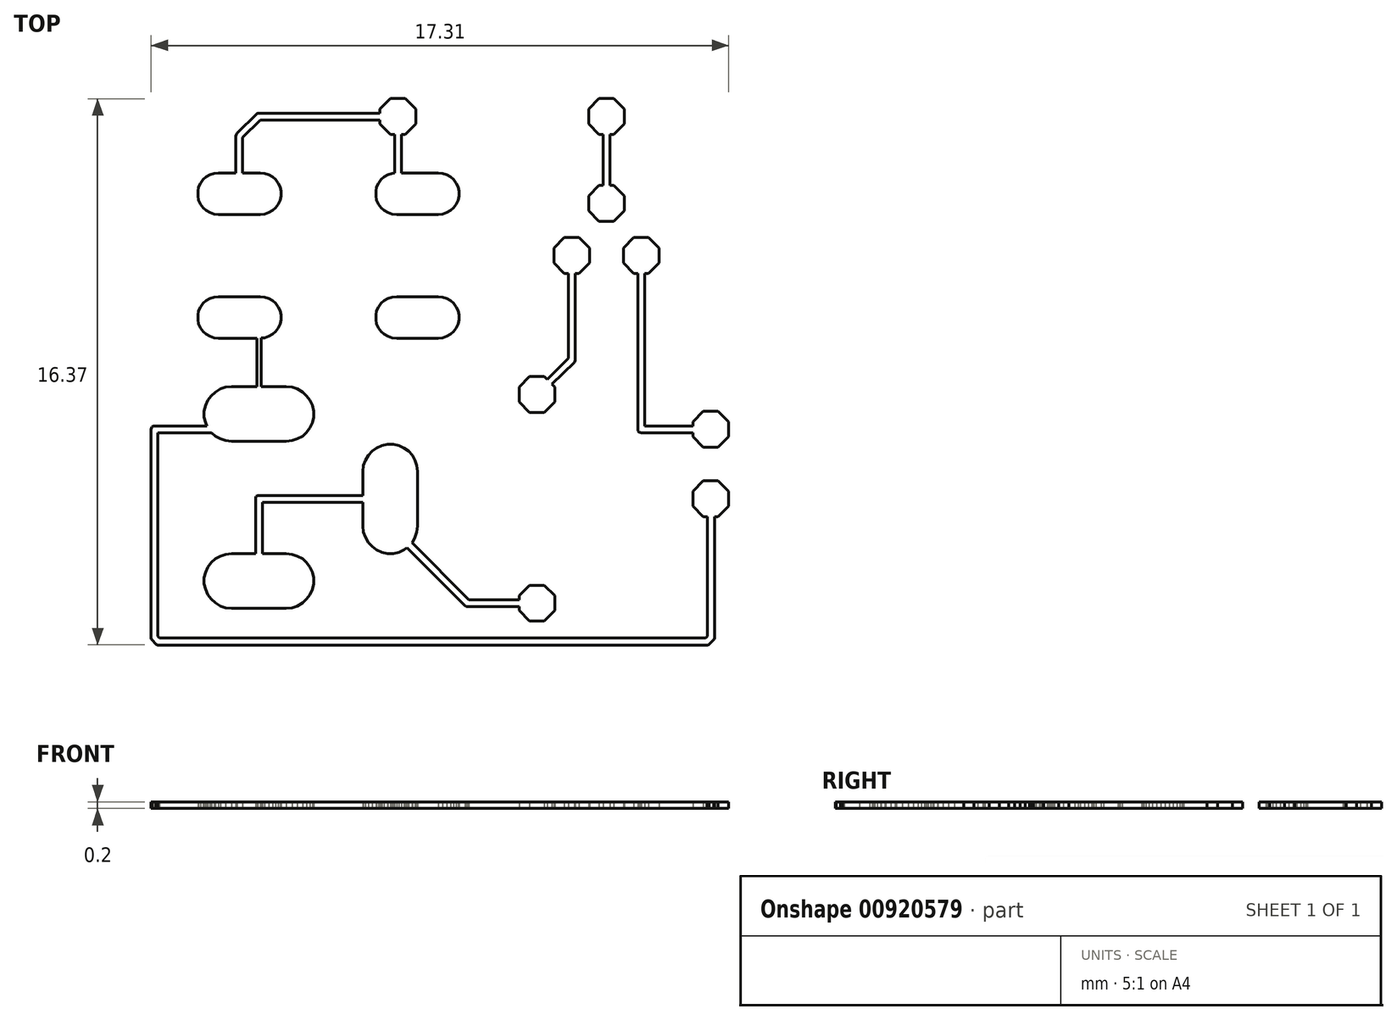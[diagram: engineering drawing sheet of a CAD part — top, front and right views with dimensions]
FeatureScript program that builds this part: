
annotation { "Feature Type Name" : "Feature", "Feature Type Description" : "" }
export const myFeature = defineFeature(function(context is Context, id is Id, definition is map)
    precondition{}
    {
        {
            var Q0;
            Q0=qCreatedBy(makeId("Top.planeOp"),FACE);
            var sketch = newSketch(context, id + "F0", { "sketchPlane" : qUnion([Q0])});
            skLineSegment(sketch, "E0", {"start": v(-0.87, 0.65) * mm, "end": v(-2.12, 0.65) * mm});
            skLineSegment(sketch, "E1", {"start": v(-2.12, 0.65) * mm, "end": v(-2.26, 0.67) * mm});
            skLineSegment(sketch, "E2", {"start": v(-2.26, 0.67) * mm, "end": v(-2.38, 0.7) * mm});
            skLineSegment(sketch, "E3", {"start": v(-2.38, 0.7) * mm, "end": v(-2.5, 0.77) * mm});
            skLineSegment(sketch, "E4", {"start": v(-2.5, 0.77) * mm, "end": v(-2.59, 0.85) * mm});
            skLineSegment(sketch, "E5", {"start": v(-2.59, 0.85) * mm, "end": v(-2.66, 0.96) * mm});
            skLineSegment(sketch, "E6", {"start": v(-2.66, 0.96) * mm, "end": v(-2.72, 1.08) * mm});
            skLineSegment(sketch, "E7", {"start": v(-2.72, 1.08) * mm, "end": v(-2.74, 1.2) * mm});
            skLineSegment(sketch, "E8", {"start": v(-2.74, 1.2) * mm, "end": v(-2.74, 1.34) * mm});
            skLineSegment(sketch, "E9", {"start": v(-2.74, 1.34) * mm, "end": v(-2.72, 1.47) * mm});
            skLineSegment(sketch, "E10", {"start": v(-2.72, 1.47) * mm, "end": v(-2.66, 1.58) * mm});
            skLineSegment(sketch, "E11", {"start": v(-2.66, 1.58) * mm, "end": v(-2.59, 1.7) * mm});
            skLineSegment(sketch, "E12", {"start": v(-2.59, 1.7) * mm, "end": v(-2.5, 1.78) * mm});
            skLineSegment(sketch, "E13", {"start": v(-2.5, 1.78) * mm, "end": v(-2.38, 1.84) * mm});
            skLineSegment(sketch, "E14", {"start": v(-2.38, 1.84) * mm, "end": v(-2.26, 1.89) * mm});
            skLineSegment(sketch, "E15", {"start": v(-2.26, 1.89) * mm, "end": v(-2.12, 1.9) * mm});
            skLineSegment(sketch, "E16", {"start": v(-2.12, 1.9) * mm, "end": v(-0.87, 1.9) * mm});
            skLineSegment(sketch, "E17", {"start": v(-0.87, 1.9) * mm, "end": v(-0.74, 1.89) * mm});
            skLineSegment(sketch, "E18", {"start": v(-0.74, 1.89) * mm, "end": v(-0.62, 1.84) * mm});
            skLineSegment(sketch, "E19", {"start": v(-0.62, 1.84) * mm, "end": v(-0.5, 1.78) * mm});
            skLineSegment(sketch, "E20", {"start": v(-0.5, 1.78) * mm, "end": v(-0.41, 1.7) * mm});
            skLineSegment(sketch, "E21", {"start": v(-0.41, 1.7) * mm, "end": v(-0.34, 1.58) * mm});
            skLineSegment(sketch, "E22", {"start": v(-0.34, 1.58) * mm, "end": v(-0.28, 1.47) * mm});
            skLineSegment(sketch, "E23", {"start": v(-0.28, 1.47) * mm, "end": v(-0.26, 1.34) * mm});
            skLineSegment(sketch, "E24", {"start": v(-0.26, 1.34) * mm, "end": v(-0.26, 1.2) * mm});
            skLineSegment(sketch, "E25", {"start": v(-0.26, 1.2) * mm, "end": v(-0.28, 1.08) * mm});
            skLineSegment(sketch, "E26", {"start": v(-0.28, 1.08) * mm, "end": v(-0.34, 0.96) * mm});
            skLineSegment(sketch, "E27", {"start": v(-0.34, 0.96) * mm, "end": v(-0.41, 0.85) * mm});
            skLineSegment(sketch, "E28", {"start": v(-0.41, 0.85) * mm, "end": v(-0.5, 0.77) * mm});
            skLineSegment(sketch, "E29", {"start": v(-0.5, 0.77) * mm, "end": v(-0.62, 0.7) * mm});
            skLineSegment(sketch, "E30", {"start": v(-0.62, 0.7) * mm, "end": v(-0.74, 0.67) * mm});
            skLineSegment(sketch, "E31", {"start": v(-0.74, 0.67) * mm, "end": v(-0.87, 0.65) * mm});
            skLineSegment(sketch, "E32", {"start": v(-10.42, 9.48) * mm, "end": v(10.45, 9.48) * mm});
            skLineSegment(sketch, "E33", {"start": v(10.45, 9.48) * mm, "end": v(10.5, 9.46) * mm});
            skLineSegment(sketch, "E34", {"start": v(10.5, 9.46) * mm, "end": v(10.52, 9.42) * mm});
            skLineSegment(sketch, "E35", {"start": v(10.52, 9.42) * mm, "end": v(10.52, -9.4) * mm});
            skLineSegment(sketch, "E36", {"start": v(10.52, -9.4) * mm, "end": v(10.5, -9.45) * mm});
            skLineSegment(sketch, "E37", {"start": v(10.5, -9.45) * mm, "end": v(10.45, -9.47) * mm});
            skLineSegment(sketch, "E38", {"start": v(10.45, -9.47) * mm, "end": v(10.41, -9.48) * mm});
            skLineSegment(sketch, "E39", {"start": v(10.41, -9.48) * mm, "end": v(-10.42, -9.48) * mm});
            skLineSegment(sketch, "E40", {"start": v(-10.42, -9.48) * mm, "end": v(-10.45, -9.47) * mm});
            skLineSegment(sketch, "E41", {"start": v(-10.45, -9.47) * mm, "end": v(-10.5, -9.45) * mm});
            skLineSegment(sketch, "E42", {"start": v(-10.5, -9.45) * mm, "end": v(-10.52, -9.4) * mm});
            skLineSegment(sketch, "E43", {"start": v(-10.52, -9.4) * mm, "end": v(-10.52, 9.43) * mm});
            skLineSegment(sketch, "E44", {"start": v(-10.52, 9.43) * mm, "end": v(-10.47, 9.47) * mm});
            skLineSegment(sketch, "E45", {"start": v(-10.47, 9.47) * mm, "end": v(-10.45, 9.48) * mm});
            skLineSegment(sketch, "E46", {"start": v(-10.45, 9.48) * mm, "end": v(-10.42, 9.48) * mm});
            skLineSegment(sketch, "E47", {"start": v(-10.32, -9.27) * mm, "end": v(10.3, -9.27) * mm});
            skLineSegment(sketch, "E48", {"start": v(10.3, -9.27) * mm, "end": v(10.3, 9.27) * mm});
            skLineSegment(sketch, "E49", {"start": v(10.3, 9.27) * mm, "end": v(-10.32, 9.27) * mm});
            skLineSegment(sketch, "E50", {"start": v(-10.32, 9.27) * mm, "end": v(-10.32, -9.27) * mm});
            skLineSegment(sketch, "E51", {"start": v(2.54, -0.73) * mm, "end": v(2.62, -0.81) * mm});
            skLineSegment(sketch, "E52", {"start": v(2.62, -0.81) * mm, "end": v(2.62, -1.26) * mm});
            skLineSegment(sketch, "E53", {"start": v(2.62, -1.26) * mm, "end": v(2.3, -1.57) * mm});
            skLineSegment(sketch, "E54", {"start": v(2.3, -1.57) * mm, "end": v(1.86, -1.57) * mm});
            skLineSegment(sketch, "E55", {"start": v(1.86, -1.57) * mm, "end": v(1.55, -1.26) * mm});
            skLineSegment(sketch, "E56", {"start": v(1.55, -1.26) * mm, "end": v(1.55, -0.81) * mm});
            skLineSegment(sketch, "E57", {"start": v(1.55, -0.81) * mm, "end": v(1.86, -0.5) * mm});
            skLineSegment(sketch, "E58", {"start": v(1.86, -0.5) * mm, "end": v(2.3, -0.5) * mm});
            skLineSegment(sketch, "E59", {"start": v(2.3, -0.5) * mm, "end": v(2.4, -0.58) * mm});
            skLineSegment(sketch, "E60", {"start": v(2.4, -0.58) * mm, "end": v(3.03, 0.05) * mm});
            skLineSegment(sketch, "E61", {"start": v(3.03, 0.05) * mm, "end": v(3.03, 2.6) * mm});
            skLineSegment(sketch, "E62", {"start": v(3.03, 2.6) * mm, "end": v(2.9, 2.6) * mm});
            skLineSegment(sketch, "E63", {"start": v(2.9, 2.6) * mm, "end": v(2.59, 2.9) * mm});
            skLineSegment(sketch, "E64", {"start": v(2.59, 2.9) * mm, "end": v(2.59, 3.35) * mm});
            skLineSegment(sketch, "E65", {"start": v(2.59, 3.35) * mm, "end": v(2.9, 3.67) * mm});
            skLineSegment(sketch, "E66", {"start": v(2.9, 3.67) * mm, "end": v(3.35, 3.67) * mm});
            skLineSegment(sketch, "E67", {"start": v(3.35, 3.67) * mm, "end": v(3.66, 3.35) * mm});
            skLineSegment(sketch, "E68", {"start": v(3.66, 3.35) * mm, "end": v(3.66, 2.9) * mm});
            skLineSegment(sketch, "E69", {"start": v(3.66, 2.9) * mm, "end": v(3.35, 2.6) * mm});
            skLineSegment(sketch, "E70", {"start": v(3.35, 2.6) * mm, "end": v(3.23, 2.6) * mm});
            skLineSegment(sketch, "E71", {"start": v(3.23, 2.6) * mm, "end": v(3.22, -0.01) * mm});
            skLineSegment(sketch, "E72", {"start": v(3.22, -0.01) * mm, "end": v(3.21, -0.05) * mm});
            skLineSegment(sketch, "E73", {"start": v(3.21, -0.05) * mm, "end": v(3.2, -0.07) * mm});
            skLineSegment(sketch, "E74", {"start": v(3.2, -0.07) * mm, "end": v(2.54, -0.73) * mm});
            skLineSegment(sketch, "E75", {"start": v(5.1, 2.6) * mm, "end": v(4.98, 2.6) * mm});
            skLineSegment(sketch, "E76", {"start": v(4.98, 2.6) * mm, "end": v(4.67, 2.9) * mm});
            skLineSegment(sketch, "E77", {"start": v(4.67, 2.9) * mm, "end": v(4.67, 3.35) * mm});
            skLineSegment(sketch, "E78", {"start": v(4.67, 3.35) * mm, "end": v(4.98, 3.67) * mm});
            skLineSegment(sketch, "E79", {"start": v(4.98, 3.67) * mm, "end": v(5.43, 3.67) * mm});
            skLineSegment(sketch, "E80", {"start": v(5.43, 3.67) * mm, "end": v(5.74, 3.35) * mm});
            skLineSegment(sketch, "E81", {"start": v(5.74, 3.35) * mm, "end": v(5.74, 2.9) * mm});
            skLineSegment(sketch, "E82", {"start": v(5.74, 2.9) * mm, "end": v(5.43, 2.6) * mm});
            skLineSegment(sketch, "E83", {"start": v(5.43, 2.6) * mm, "end": v(5.32, 2.6) * mm});
            skLineSegment(sketch, "E84", {"start": v(5.32, 2.6) * mm, "end": v(5.32, -1.98) * mm});
            skLineSegment(sketch, "E85", {"start": v(5.32, -1.98) * mm, "end": v(6.76, -1.98) * mm});
            skLineSegment(sketch, "E86", {"start": v(6.76, -1.98) * mm, "end": v(6.76, -1.85) * mm});
            skLineSegment(sketch, "E87", {"start": v(6.76, -1.85) * mm, "end": v(7.07, -1.54) * mm});
            skLineSegment(sketch, "E88", {"start": v(7.07, -1.54) * mm, "end": v(7.52, -1.54) * mm});
            skLineSegment(sketch, "E89", {"start": v(7.52, -1.54) * mm, "end": v(7.83, -1.85) * mm});
            skLineSegment(sketch, "E90", {"start": v(7.83, -1.85) * mm, "end": v(7.83, -2.3) * mm});
            skLineSegment(sketch, "E91", {"start": v(7.83, -2.3) * mm, "end": v(7.52, -2.61) * mm});
            skLineSegment(sketch, "E92", {"start": v(7.52, -2.61) * mm, "end": v(7.07, -2.61) * mm});
            skLineSegment(sketch, "E93", {"start": v(7.07, -2.61) * mm, "end": v(6.76, -2.3) * mm});
            skLineSegment(sketch, "E94", {"start": v(6.76, -2.3) * mm, "end": v(6.76, -2.19) * mm});
            skLineSegment(sketch, "E95", {"start": v(6.76, -2.19) * mm, "end": v(5.21, -2.19) * mm});
            skLineSegment(sketch, "E96", {"start": v(5.21, -2.19) * mm, "end": v(5.17, -2.18) * mm});
            skLineSegment(sketch, "E97", {"start": v(5.17, -2.18) * mm, "end": v(5.13, -2.16) * mm});
            skLineSegment(sketch, "E98", {"start": v(5.13, -2.16) * mm, "end": v(5.1, -2.11) * mm});
            skLineSegment(sketch, "E99", {"start": v(5.1, -2.11) * mm, "end": v(5.1, 2.6) * mm});
            skLineSegment(sketch, "E100", {"start": v(4.07, 5.23) * mm, "end": v(4.07, 6.76) * mm});
            skLineSegment(sketch, "E101", {"start": v(4.07, 6.76) * mm, "end": v(3.94, 6.76) * mm});
            skLineSegment(sketch, "E102", {"start": v(3.94, 6.76) * mm, "end": v(3.63, 7.07) * mm});
            skLineSegment(sketch, "E103", {"start": v(3.63, 7.07) * mm, "end": v(3.63, 7.52) * mm});
            skLineSegment(sketch, "E104", {"start": v(3.63, 7.52) * mm, "end": v(3.94, 7.83) * mm});
            skLineSegment(sketch, "E105", {"start": v(3.94, 7.83) * mm, "end": v(4.4, 7.83) * mm});
            skLineSegment(sketch, "E106", {"start": v(4.4, 7.83) * mm, "end": v(4.7, 7.52) * mm});
            skLineSegment(sketch, "E107", {"start": v(4.7, 7.52) * mm, "end": v(4.7, 7.07) * mm});
            skLineSegment(sketch, "E108", {"start": v(4.7, 7.07) * mm, "end": v(4.4, 6.76) * mm});
            skLineSegment(sketch, "E109", {"start": v(4.4, 6.76) * mm, "end": v(4.28, 6.76) * mm});
            skLineSegment(sketch, "E110", {"start": v(4.28, 6.76) * mm, "end": v(4.28, 5.23) * mm});
            skLineSegment(sketch, "E111", {"start": v(4.28, 5.23) * mm, "end": v(4.4, 5.23) * mm});
            skLineSegment(sketch, "E112", {"start": v(4.4, 5.23) * mm, "end": v(4.7, 4.92) * mm});
            skLineSegment(sketch, "E113", {"start": v(4.7, 4.92) * mm, "end": v(4.7, 4.47) * mm});
            skLineSegment(sketch, "E114", {"start": v(4.7, 4.47) * mm, "end": v(4.4, 4.16) * mm});
            skLineSegment(sketch, "E115", {"start": v(4.4, 4.16) * mm, "end": v(3.94, 4.16) * mm});
            skLineSegment(sketch, "E116", {"start": v(3.94, 4.16) * mm, "end": v(3.63, 4.47) * mm});
            skLineSegment(sketch, "E117", {"start": v(3.63, 4.47) * mm, "end": v(3.63, 4.92) * mm});
            skLineSegment(sketch, "E118", {"start": v(3.63, 4.92) * mm, "end": v(3.94, 5.23) * mm});
            skLineSegment(sketch, "E119", {"start": v(3.94, 5.23) * mm, "end": v(4.07, 5.23) * mm});
            skLineSegment(sketch, "E120", {"start": v(-6.73, 5.6) * mm, "end": v(-6.2, 5.6) * mm});
            skLineSegment(sketch, "E121", {"start": v(-6.2, 5.6) * mm, "end": v(-6.08, 5.6) * mm});
            skLineSegment(sketch, "E122", {"start": v(-6.08, 5.6) * mm, "end": v(-5.95, 5.55) * mm});
            skLineSegment(sketch, "E123", {"start": v(-5.95, 5.55) * mm, "end": v(-5.84, 5.49) * mm});
            skLineSegment(sketch, "E124", {"start": v(-5.84, 5.49) * mm, "end": v(-5.74, 5.4) * mm});
            skLineSegment(sketch, "E125", {"start": v(-5.74, 5.4) * mm, "end": v(-5.67, 5.3) * mm});
            skLineSegment(sketch, "E126", {"start": v(-5.67, 5.3) * mm, "end": v(-5.6, 5.18) * mm});
            skLineSegment(sketch, "E127", {"start": v(-5.6, 5.18) * mm, "end": v(-5.59, 5.05) * mm});
            skLineSegment(sketch, "E128", {"start": v(-5.59, 5.05) * mm, "end": v(-5.59, 4.92) * mm});
            skLineSegment(sketch, "E129", {"start": v(-5.59, 4.92) * mm, "end": v(-5.6, 4.8) * mm});
            skLineSegment(sketch, "E130", {"start": v(-5.6, 4.8) * mm, "end": v(-5.67, 4.67) * mm});
            skLineSegment(sketch, "E131", {"start": v(-5.67, 4.67) * mm, "end": v(-5.74, 4.56) * mm});
            skLineSegment(sketch, "E132", {"start": v(-5.74, 4.56) * mm, "end": v(-5.84, 4.48) * mm});
            skLineSegment(sketch, "E133", {"start": v(-5.84, 4.48) * mm, "end": v(-5.95, 4.42) * mm});
            skLineSegment(sketch, "E134", {"start": v(-5.95, 4.42) * mm, "end": v(-6.08, 4.38) * mm});
            skLineSegment(sketch, "E135", {"start": v(-6.08, 4.38) * mm, "end": v(-6.2, 4.35) * mm});
            skLineSegment(sketch, "E136", {"start": v(-6.2, 4.35) * mm, "end": v(-7.46, 4.35) * mm});
            skLineSegment(sketch, "E137", {"start": v(-7.46, 4.35) * mm, "end": v(-7.59, 4.38) * mm});
            skLineSegment(sketch, "E138", {"start": v(-7.59, 4.38) * mm, "end": v(-7.71, 4.42) * mm});
            skLineSegment(sketch, "E139", {"start": v(-7.71, 4.42) * mm, "end": v(-7.83, 4.48) * mm});
            skLineSegment(sketch, "E140", {"start": v(-7.83, 4.48) * mm, "end": v(-7.92, 4.56) * mm});
            skLineSegment(sketch, "E141", {"start": v(-7.92, 4.56) * mm, "end": v(-8, 4.67) * mm});
            skLineSegment(sketch, "E142", {"start": v(-8, 4.67) * mm, "end": v(-8.06, 4.8) * mm});
            skLineSegment(sketch, "E143", {"start": v(-8.06, 4.8) * mm, "end": v(-8.08, 4.92) * mm});
            skLineSegment(sketch, "E144", {"start": v(-8.08, 4.92) * mm, "end": v(-8.08, 5.05) * mm});
            skLineSegment(sketch, "E145", {"start": v(-8.08, 5.05) * mm, "end": v(-8.06, 5.18) * mm});
            skLineSegment(sketch, "E146", {"start": v(-8.06, 5.18) * mm, "end": v(-8, 5.3) * mm});
            skLineSegment(sketch, "E147", {"start": v(-8, 5.3) * mm, "end": v(-7.92, 5.4) * mm});
            skLineSegment(sketch, "E148", {"start": v(-7.92, 5.4) * mm, "end": v(-7.83, 5.49) * mm});
            skLineSegment(sketch, "E149", {"start": v(-7.83, 5.49) * mm, "end": v(-7.71, 5.55) * mm});
            skLineSegment(sketch, "E150", {"start": v(-7.71, 5.55) * mm, "end": v(-7.59, 5.6) * mm});
            skLineSegment(sketch, "E151", {"start": v(-7.59, 5.6) * mm, "end": v(-7.46, 5.6) * mm});
            skLineSegment(sketch, "E152", {"start": v(-7.46, 5.6) * mm, "end": v(-6.94, 5.6) * mm});
            skLineSegment(sketch, "E153", {"start": v(-6.94, 5.6) * mm, "end": v(-6.94, 6.7) * mm});
            skLineSegment(sketch, "E154", {"start": v(-6.94, 6.7) * mm, "end": v(-6.93, 6.75) * mm});
            skLineSegment(sketch, "E155", {"start": v(-6.93, 6.75) * mm, "end": v(-6.91, 6.8) * mm});
            skLineSegment(sketch, "E156", {"start": v(-6.91, 6.8) * mm, "end": v(-6.3, 7.39) * mm});
            skLineSegment(sketch, "E157", {"start": v(-6.3, 7.39) * mm, "end": v(-6.29, 7.4) * mm});
            skLineSegment(sketch, "E158", {"start": v(-6.29, 7.4) * mm, "end": v(-2.62, 7.4) * mm});
            skLineSegment(sketch, "E159", {"start": v(-2.62, 7.4) * mm, "end": v(-2.62, 7.52) * mm});
            skLineSegment(sketch, "E160", {"start": v(-2.62, 7.52) * mm, "end": v(-2.3, 7.83) * mm});
            skLineSegment(sketch, "E161", {"start": v(-2.3, 7.83) * mm, "end": v(-1.86, 7.83) * mm});
            skLineSegment(sketch, "E162", {"start": v(-1.86, 7.83) * mm, "end": v(-1.55, 7.52) * mm});
            skLineSegment(sketch, "E163", {"start": v(-1.55, 7.52) * mm, "end": v(-1.55, 7.07) * mm});
            skLineSegment(sketch, "E164", {"start": v(-1.55, 7.07) * mm, "end": v(-1.86, 6.76) * mm});
            skLineSegment(sketch, "E165", {"start": v(-1.86, 6.76) * mm, "end": v(-1.97, 6.76) * mm});
            skLineSegment(sketch, "E166", {"start": v(-1.97, 6.76) * mm, "end": v(-1.97, 5.6) * mm});
            skLineSegment(sketch, "E167", {"start": v(-1.97, 5.6) * mm, "end": v(-0.87, 5.6) * mm});
            skLineSegment(sketch, "E168", {"start": v(-0.87, 5.6) * mm, "end": v(-0.74, 5.6) * mm});
            skLineSegment(sketch, "E169", {"start": v(-0.74, 5.6) * mm, "end": v(-0.62, 5.55) * mm});
            skLineSegment(sketch, "E170", {"start": v(-0.62, 5.55) * mm, "end": v(-0.5, 5.49) * mm});
            skLineSegment(sketch, "E171", {"start": v(-0.5, 5.49) * mm, "end": v(-0.41, 5.4) * mm});
            skLineSegment(sketch, "E172", {"start": v(-0.41, 5.4) * mm, "end": v(-0.34, 5.3) * mm});
            skLineSegment(sketch, "E173", {"start": v(-0.34, 5.3) * mm, "end": v(-0.28, 5.18) * mm});
            skLineSegment(sketch, "E174", {"start": v(-0.28, 5.18) * mm, "end": v(-0.26, 5.05) * mm});
            skLineSegment(sketch, "E175", {"start": v(-0.26, 5.05) * mm, "end": v(-0.26, 4.92) * mm});
            skLineSegment(sketch, "E176", {"start": v(-0.26, 4.92) * mm, "end": v(-0.28, 4.8) * mm});
            skLineSegment(sketch, "E177", {"start": v(-0.28, 4.8) * mm, "end": v(-0.34, 4.67) * mm});
            skLineSegment(sketch, "E178", {"start": v(-0.34, 4.67) * mm, "end": v(-0.41, 4.56) * mm});
            skLineSegment(sketch, "E179", {"start": v(-0.41, 4.56) * mm, "end": v(-0.5, 4.48) * mm});
            skLineSegment(sketch, "E180", {"start": v(-0.5, 4.48) * mm, "end": v(-0.62, 4.42) * mm});
            skLineSegment(sketch, "E181", {"start": v(-0.62, 4.42) * mm, "end": v(-0.74, 4.38) * mm});
            skLineSegment(sketch, "E182", {"start": v(-0.74, 4.38) * mm, "end": v(-0.87, 4.35) * mm});
            skLineSegment(sketch, "E183", {"start": v(-0.87, 4.35) * mm, "end": v(-2.12, 4.35) * mm});
            skLineSegment(sketch, "E184", {"start": v(-2.12, 4.35) * mm, "end": v(-2.26, 4.38) * mm});
            skLineSegment(sketch, "E185", {"start": v(-2.26, 4.38) * mm, "end": v(-2.38, 4.42) * mm});
            skLineSegment(sketch, "E186", {"start": v(-2.38, 4.42) * mm, "end": v(-2.5, 4.48) * mm});
            skLineSegment(sketch, "E187", {"start": v(-2.5, 4.48) * mm, "end": v(-2.59, 4.56) * mm});
            skLineSegment(sketch, "E188", {"start": v(-2.59, 4.56) * mm, "end": v(-2.66, 4.67) * mm});
            skLineSegment(sketch, "E189", {"start": v(-2.66, 4.67) * mm, "end": v(-2.72, 4.8) * mm});
            skLineSegment(sketch, "E190", {"start": v(-2.72, 4.8) * mm, "end": v(-2.74, 4.92) * mm});
            skLineSegment(sketch, "E191", {"start": v(-2.74, 4.92) * mm, "end": v(-2.74, 5.05) * mm});
            skLineSegment(sketch, "E192", {"start": v(-2.74, 5.05) * mm, "end": v(-2.72, 5.18) * mm});
            skLineSegment(sketch, "E193", {"start": v(-2.72, 5.18) * mm, "end": v(-2.66, 5.3) * mm});
            skLineSegment(sketch, "E194", {"start": v(-2.66, 5.3) * mm, "end": v(-2.59, 5.4) * mm});
            skLineSegment(sketch, "E195", {"start": v(-2.59, 5.4) * mm, "end": v(-2.5, 5.49) * mm});
            skLineSegment(sketch, "E196", {"start": v(-2.5, 5.49) * mm, "end": v(-2.38, 5.55) * mm});
            skLineSegment(sketch, "E197", {"start": v(-2.38, 5.55) * mm, "end": v(-2.26, 5.6) * mm});
            skLineSegment(sketch, "E198", {"start": v(-2.26, 5.6) * mm, "end": v(-2.18, 5.6) * mm});
            skLineSegment(sketch, "E199", {"start": v(-2.18, 5.6) * mm, "end": v(-2.18, 6.76) * mm});
            skLineSegment(sketch, "E200", {"start": v(-2.18, 6.76) * mm, "end": v(-2.3, 6.76) * mm});
            skLineSegment(sketch, "E201", {"start": v(-2.3, 6.76) * mm, "end": v(-2.62, 7.07) * mm});
            skLineSegment(sketch, "E202", {"start": v(-2.62, 7.07) * mm, "end": v(-2.62, 7.19) * mm});
            skLineSegment(sketch, "E203", {"start": v(-2.62, 7.19) * mm, "end": v(-6.2, 7.19) * mm});
            skLineSegment(sketch, "E204", {"start": v(-6.2, 7.19) * mm, "end": v(-6.73, 6.67) * mm});
            skLineSegment(sketch, "E205", {"start": v(-6.73, 6.67) * mm, "end": v(-6.73, 5.6) * mm});
            skLineSegment(sketch, "E206", {"start": v(-1.8, -5.62) * mm, "end": v(-1.9, -5.69) * mm});
            skLineSegment(sketch, "E207", {"start": v(-1.9, -5.69) * mm, "end": v(-2.06, -5.76) * mm});
            skLineSegment(sketch, "E208", {"start": v(-2.06, -5.76) * mm, "end": v(-2.22, -5.8) * mm});
            skLineSegment(sketch, "E209", {"start": v(-2.22, -5.8) * mm, "end": v(-2.4, -5.8) * mm});
            skLineSegment(sketch, "E210", {"start": v(-2.4, -5.8) * mm, "end": v(-2.57, -5.76) * mm});
            skLineSegment(sketch, "E211", {"start": v(-2.57, -5.76) * mm, "end": v(-2.72, -5.69) * mm});
            skLineSegment(sketch, "E212", {"start": v(-2.72, -5.69) * mm, "end": v(-2.86, -5.6) * mm});
            skLineSegment(sketch, "E213", {"start": v(-2.86, -5.6) * mm, "end": v(-2.97, -5.47) * mm});
            skLineSegment(sketch, "E214", {"start": v(-2.97, -5.47) * mm, "end": v(-3.06, -5.31) * mm});
            skLineSegment(sketch, "E215", {"start": v(-3.06, -5.31) * mm, "end": v(-3.12, -5.16) * mm});
            skLineSegment(sketch, "E216", {"start": v(-3.12, -5.16) * mm, "end": v(-3.13, -4.98) * mm});
            skLineSegment(sketch, "E217", {"start": v(-3.13, -4.98) * mm, "end": v(-3.13, -4.27) * mm});
            skLineSegment(sketch, "E218", {"start": v(-3.13, -4.27) * mm, "end": v(-6.14, -4.27) * mm});
            skLineSegment(sketch, "E219", {"start": v(-6.14, -4.27) * mm, "end": v(-6.14, -5.8) * mm});
            skLineSegment(sketch, "E220", {"start": v(-6.14, -5.8) * mm, "end": v(-5.43, -5.8) * mm});
            skLineSegment(sketch, "E221", {"start": v(-5.43, -5.8) * mm, "end": v(-5.26, -5.82) * mm});
            skLineSegment(sketch, "E222", {"start": v(-5.26, -5.82) * mm, "end": v(-5.1, -5.87) * mm});
            skLineSegment(sketch, "E223", {"start": v(-5.1, -5.87) * mm, "end": v(-4.94, -5.96) * mm});
            skLineSegment(sketch, "E224", {"start": v(-4.94, -5.96) * mm, "end": v(-4.82, -6.07) * mm});
            skLineSegment(sketch, "E225", {"start": v(-4.82, -6.07) * mm, "end": v(-4.72, -6.2) * mm});
            skLineSegment(sketch, "E226", {"start": v(-4.72, -6.2) * mm, "end": v(-4.65, -6.36) * mm});
            skLineSegment(sketch, "E227", {"start": v(-4.65, -6.36) * mm, "end": v(-4.6, -6.53) * mm});
            skLineSegment(sketch, "E228", {"start": v(-4.6, -6.53) * mm, "end": v(-4.6, -6.7) * mm});
            skLineSegment(sketch, "E229", {"start": v(-4.6, -6.7) * mm, "end": v(-4.65, -6.87) * mm});
            skLineSegment(sketch, "E230", {"start": v(-4.65, -6.87) * mm, "end": v(-4.72, -7.03) * mm});
            skLineSegment(sketch, "E231", {"start": v(-4.72, -7.03) * mm, "end": v(-4.82, -7.17) * mm});
            skLineSegment(sketch, "E232", {"start": v(-4.82, -7.17) * mm, "end": v(-4.94, -7.28) * mm});
            skLineSegment(sketch, "E233", {"start": v(-4.94, -7.28) * mm, "end": v(-5.1, -7.37) * mm});
            skLineSegment(sketch, "E234", {"start": v(-5.1, -7.37) * mm, "end": v(-5.26, -7.43) * mm});
            skLineSegment(sketch, "E235", {"start": v(-5.26, -7.43) * mm, "end": v(-5.43, -7.44) * mm});
            skLineSegment(sketch, "E236", {"start": v(-5.43, -7.44) * mm, "end": v(-7.07, -7.44) * mm});
            skLineSegment(sketch, "E237", {"start": v(-7.07, -7.44) * mm, "end": v(-7.24, -7.43) * mm});
            skLineSegment(sketch, "E238", {"start": v(-7.24, -7.43) * mm, "end": v(-7.4, -7.37) * mm});
            skLineSegment(sketch, "E239", {"start": v(-7.4, -7.37) * mm, "end": v(-7.56, -7.28) * mm});
            skLineSegment(sketch, "E240", {"start": v(-7.56, -7.28) * mm, "end": v(-7.68, -7.17) * mm});
            skLineSegment(sketch, "E241", {"start": v(-7.68, -7.17) * mm, "end": v(-7.78, -7.03) * mm});
            skLineSegment(sketch, "E242", {"start": v(-7.78, -7.03) * mm, "end": v(-7.85, -6.87) * mm});
            skLineSegment(sketch, "E243", {"start": v(-7.85, -6.87) * mm, "end": v(-7.9, -6.7) * mm});
            skLineSegment(sketch, "E244", {"start": v(-7.9, -6.7) * mm, "end": v(-7.9, -6.53) * mm});
            skLineSegment(sketch, "E245", {"start": v(-7.9, -6.53) * mm, "end": v(-7.85, -6.36) * mm});
            skLineSegment(sketch, "E246", {"start": v(-7.85, -6.36) * mm, "end": v(-7.78, -6.2) * mm});
            skLineSegment(sketch, "E247", {"start": v(-7.78, -6.2) * mm, "end": v(-7.68, -6.07) * mm});
            skLineSegment(sketch, "E248", {"start": v(-7.68, -6.07) * mm, "end": v(-7.56, -5.96) * mm});
            skLineSegment(sketch, "E249", {"start": v(-7.56, -5.96) * mm, "end": v(-7.4, -5.87) * mm});
            skLineSegment(sketch, "E250", {"start": v(-7.4, -5.87) * mm, "end": v(-7.24, -5.82) * mm});
            skLineSegment(sketch, "E251", {"start": v(-7.24, -5.82) * mm, "end": v(-7.07, -5.8) * mm});
            skLineSegment(sketch, "E252", {"start": v(-7.07, -5.8) * mm, "end": v(-6.35, -5.8) * mm});
            skLineSegment(sketch, "E253", {"start": v(-6.35, -5.8) * mm, "end": v(-6.35, -4.12) * mm});
            skLineSegment(sketch, "E254", {"start": v(-6.35, -4.12) * mm, "end": v(-6.33, -4.08) * mm});
            skLineSegment(sketch, "E255", {"start": v(-6.33, -4.08) * mm, "end": v(-6.29, -4.06) * mm});
            skLineSegment(sketch, "E256", {"start": v(-6.29, -4.06) * mm, "end": v(-3.13, -4.06) * mm});
            skLineSegment(sketch, "E257", {"start": v(-3.13, -4.06) * mm, "end": v(-3.13, -3.34) * mm});
            skLineSegment(sketch, "E258", {"start": v(-3.13, -3.34) * mm, "end": v(-3.12, -3.17) * mm});
            skLineSegment(sketch, "E259", {"start": v(-3.12, -3.17) * mm, "end": v(-3.06, -3.01) * mm});
            skLineSegment(sketch, "E260", {"start": v(-3.06, -3.01) * mm, "end": v(-2.97, -2.85) * mm});
            skLineSegment(sketch, "E261", {"start": v(-2.97, -2.85) * mm, "end": v(-2.86, -2.73) * mm});
            skLineSegment(sketch, "E262", {"start": v(-2.86, -2.73) * mm, "end": v(-2.72, -2.64) * mm});
            skLineSegment(sketch, "E263", {"start": v(-2.72, -2.64) * mm, "end": v(-2.57, -2.56) * mm});
            skLineSegment(sketch, "E264", {"start": v(-2.57, -2.56) * mm, "end": v(-2.4, -2.52) * mm});
            skLineSegment(sketch, "E265", {"start": v(-2.4, -2.52) * mm, "end": v(-2.22, -2.52) * mm});
            skLineSegment(sketch, "E266", {"start": v(-2.22, -2.52) * mm, "end": v(-2.06, -2.56) * mm});
            skLineSegment(sketch, "E267", {"start": v(-2.06, -2.56) * mm, "end": v(-1.9, -2.64) * mm});
            skLineSegment(sketch, "E268", {"start": v(-1.9, -2.64) * mm, "end": v(-1.77, -2.73) * mm});
            skLineSegment(sketch, "E269", {"start": v(-1.77, -2.73) * mm, "end": v(-1.65, -2.85) * mm});
            skLineSegment(sketch, "E270", {"start": v(-1.65, -2.85) * mm, "end": v(-1.57, -3.01) * mm});
            skLineSegment(sketch, "E271", {"start": v(-1.57, -3.01) * mm, "end": v(-1.52, -3.17) * mm});
            skLineSegment(sketch, "E272", {"start": v(-1.52, -3.17) * mm, "end": v(-1.5, -3.34) * mm});
            skLineSegment(sketch, "E273", {"start": v(-1.5, -3.34) * mm, "end": v(-1.5, -4.98) * mm});
            skLineSegment(sketch, "E274", {"start": v(-1.5, -4.98) * mm, "end": v(-1.52, -5.16) * mm});
            skLineSegment(sketch, "E275", {"start": v(-1.52, -5.16) * mm, "end": v(-1.57, -5.31) * mm});
            skLineSegment(sketch, "E276", {"start": v(-1.57, -5.31) * mm, "end": v(-1.65, -5.47) * mm});
            skLineSegment(sketch, "E277", {"start": v(-1.65, -5.47) * mm, "end": v(-1.66, -5.48) * mm});
            skLineSegment(sketch, "E278", {"start": v(-1.66, -5.48) * mm, "end": v(0.05, -7.19) * mm});
            skLineSegment(sketch, "E279", {"start": v(0.05, -7.19) * mm, "end": v(1.55, -7.19) * mm});
            skLineSegment(sketch, "E280", {"start": v(1.55, -7.19) * mm, "end": v(1.55, -7.06) * mm});
            skLineSegment(sketch, "E281", {"start": v(1.55, -7.06) * mm, "end": v(1.86, -6.75) * mm});
            skLineSegment(sketch, "E282", {"start": v(1.86, -6.75) * mm, "end": v(2.3, -6.75) * mm});
            skLineSegment(sketch, "E283", {"start": v(2.3, -6.75) * mm, "end": v(2.62, -7.06) * mm});
            skLineSegment(sketch, "E284", {"start": v(2.62, -7.06) * mm, "end": v(2.62, -7.51) * mm});
            skLineSegment(sketch, "E285", {"start": v(2.62, -7.51) * mm, "end": v(2.3, -7.82) * mm});
            skLineSegment(sketch, "E286", {"start": v(2.3, -7.82) * mm, "end": v(1.86, -7.82) * mm});
            skLineSegment(sketch, "E287", {"start": v(1.86, -7.82) * mm, "end": v(1.55, -7.51) * mm});
            skLineSegment(sketch, "E288", {"start": v(1.55, -7.51) * mm, "end": v(1.55, -7.4) * mm});
            skLineSegment(sketch, "E289", {"start": v(1.55, -7.4) * mm, "end": v(0, -7.4) * mm});
            skLineSegment(sketch, "E290", {"start": v(0, -7.4) * mm, "end": v(-0.04, -7.39) * mm});
            skLineSegment(sketch, "E291", {"start": v(-0.04, -7.39) * mm, "end": v(-0.08, -7.36) * mm});
            skLineSegment(sketch, "E292", {"start": v(-0.08, -7.36) * mm, "end": v(-1.8, -5.62) * mm});
            skLineSegment(sketch, "E293", {"start": v(-6.18, -0.8) * mm, "end": v(-5.43, -0.8) * mm});
            skLineSegment(sketch, "E294", {"start": v(-5.43, -0.8) * mm, "end": v(-5.26, -0.81) * mm});
            skLineSegment(sketch, "E295", {"start": v(-5.26, -0.81) * mm, "end": v(-5.1, -0.86) * mm});
            skLineSegment(sketch, "E296", {"start": v(-5.1, -0.86) * mm, "end": v(-4.94, -0.96) * mm});
            skLineSegment(sketch, "E297", {"start": v(-4.94, -0.96) * mm, "end": v(-4.82, -1.07) * mm});
            skLineSegment(sketch, "E298", {"start": v(-4.82, -1.07) * mm, "end": v(-4.72, -1.2) * mm});
            skLineSegment(sketch, "E299", {"start": v(-4.72, -1.2) * mm, "end": v(-4.65, -1.36) * mm});
            skLineSegment(sketch, "E300", {"start": v(-4.65, -1.36) * mm, "end": v(-4.6, -1.53) * mm});
            skLineSegment(sketch, "E301", {"start": v(-4.6, -1.53) * mm, "end": v(-4.6, -1.7) * mm});
            skLineSegment(sketch, "E302", {"start": v(-4.6, -1.7) * mm, "end": v(-4.65, -1.87) * mm});
            skLineSegment(sketch, "E303", {"start": v(-4.65, -1.87) * mm, "end": v(-4.72, -2.03) * mm});
            skLineSegment(sketch, "E304", {"start": v(-4.72, -2.03) * mm, "end": v(-4.82, -2.17) * mm});
            skLineSegment(sketch, "E305", {"start": v(-4.82, -2.17) * mm, "end": v(-4.94, -2.28) * mm});
            skLineSegment(sketch, "E306", {"start": v(-4.94, -2.28) * mm, "end": v(-5.1, -2.36) * mm});
            skLineSegment(sketch, "E307", {"start": v(-5.1, -2.36) * mm, "end": v(-5.26, -2.42) * mm});
            skLineSegment(sketch, "E308", {"start": v(-5.26, -2.42) * mm, "end": v(-5.43, -2.44) * mm});
            skLineSegment(sketch, "E309", {"start": v(-5.43, -2.44) * mm, "end": v(-7.07, -2.44) * mm});
            skLineSegment(sketch, "E310", {"start": v(-7.07, -2.44) * mm, "end": v(-7.24, -2.42) * mm});
            skLineSegment(sketch, "E311", {"start": v(-7.24, -2.42) * mm, "end": v(-7.4, -2.36) * mm});
            skLineSegment(sketch, "E312", {"start": v(-7.4, -2.36) * mm, "end": v(-7.56, -2.28) * mm});
            skLineSegment(sketch, "E313", {"start": v(-7.56, -2.28) * mm, "end": v(-7.66, -2.19) * mm});
            skLineSegment(sketch, "E314", {"start": v(-7.66, -2.19) * mm, "end": v(-9.28, -2.19) * mm});
            skLineSegment(sketch, "E315", {"start": v(-9.28, -2.19) * mm, "end": v(-9.28, -8.28) * mm});
            skLineSegment(sketch, "E316", {"start": v(-9.28, -8.28) * mm, "end": v(-9.22, -8.33) * mm});
            skLineSegment(sketch, "E317", {"start": v(-9.22, -8.33) * mm, "end": v(7.14, -8.33) * mm});
            skLineSegment(sketch, "E318", {"start": v(7.14, -8.33) * mm, "end": v(7.2, -8.28) * mm});
            skLineSegment(sketch, "E319", {"start": v(7.2, -8.28) * mm, "end": v(7.2, -4.7) * mm});
            skLineSegment(sketch, "E320", {"start": v(7.2, -4.7) * mm, "end": v(7.07, -4.7) * mm});
            skLineSegment(sketch, "E321", {"start": v(7.07, -4.7) * mm, "end": v(6.76, -4.39) * mm});
            skLineSegment(sketch, "E322", {"start": v(6.76, -4.39) * mm, "end": v(6.76, -3.94) * mm});
            skLineSegment(sketch, "E323", {"start": v(6.76, -3.94) * mm, "end": v(7.07, -3.62) * mm});
            skLineSegment(sketch, "E324", {"start": v(7.07, -3.62) * mm, "end": v(7.52, -3.62) * mm});
            skLineSegment(sketch, "E325", {"start": v(7.52, -3.62) * mm, "end": v(7.83, -3.94) * mm});
            skLineSegment(sketch, "E326", {"start": v(7.83, -3.94) * mm, "end": v(7.83, -4.39) * mm});
            skLineSegment(sketch, "E327", {"start": v(7.83, -4.39) * mm, "end": v(7.52, -4.7) * mm});
            skLineSegment(sketch, "E328", {"start": v(7.52, -4.7) * mm, "end": v(7.4, -4.7) * mm});
            skLineSegment(sketch, "E329", {"start": v(7.4, -4.7) * mm, "end": v(7.4, -8.33) * mm});
            skLineSegment(sketch, "E330", {"start": v(7.4, -8.33) * mm, "end": v(7.4, -8.36) * mm});
            skLineSegment(sketch, "E331", {"start": v(7.4, -8.36) * mm, "end": v(7.38, -8.39) * mm});
            skLineSegment(sketch, "E332", {"start": v(7.38, -8.39) * mm, "end": v(7.24, -8.52) * mm});
            skLineSegment(sketch, "E333", {"start": v(7.24, -8.52) * mm, "end": v(7.22, -8.53) * mm});
            skLineSegment(sketch, "E334", {"start": v(7.22, -8.53) * mm, "end": v(7.2, -8.54) * mm});
            skLineSegment(sketch, "E335", {"start": v(7.2, -8.54) * mm, "end": v(-9.28, -8.54) * mm});
            skLineSegment(sketch, "E336", {"start": v(-9.28, -8.54) * mm, "end": v(-9.3, -8.53) * mm});
            skLineSegment(sketch, "E337", {"start": v(-9.3, -8.53) * mm, "end": v(-9.33, -8.52) * mm});
            skLineSegment(sketch, "E338", {"start": v(-9.33, -8.52) * mm, "end": v(-9.46, -8.39) * mm});
            skLineSegment(sketch, "E339", {"start": v(-9.46, -8.39) * mm, "end": v(-9.47, -8.36) * mm});
            skLineSegment(sketch, "E340", {"start": v(-9.47, -8.36) * mm, "end": v(-9.48, -8.33) * mm});
            skLineSegment(sketch, "E341", {"start": v(-9.48, -8.33) * mm, "end": v(-9.48, -2.08) * mm});
            skLineSegment(sketch, "E342", {"start": v(-9.48, -2.08) * mm, "end": v(-9.47, -2.04) * mm});
            skLineSegment(sketch, "E343", {"start": v(-9.47, -2.04) * mm, "end": v(-9.45, -2) * mm});
            skLineSegment(sketch, "E344", {"start": v(-9.45, -2) * mm, "end": v(-9.41, -1.98) * mm});
            skLineSegment(sketch, "E345", {"start": v(-9.41, -1.98) * mm, "end": v(-7.8, -1.98) * mm});
            skLineSegment(sketch, "E346", {"start": v(-7.8, -1.98) * mm, "end": v(-7.85, -1.87) * mm});
            skLineSegment(sketch, "E347", {"start": v(-7.85, -1.87) * mm, "end": v(-7.9, -1.7) * mm});
            skLineSegment(sketch, "E348", {"start": v(-7.9, -1.7) * mm, "end": v(-7.9, -1.53) * mm});
            skLineSegment(sketch, "E349", {"start": v(-7.9, -1.53) * mm, "end": v(-7.85, -1.36) * mm});
            skLineSegment(sketch, "E350", {"start": v(-7.85, -1.36) * mm, "end": v(-7.78, -1.2) * mm});
            skLineSegment(sketch, "E351", {"start": v(-7.78, -1.2) * mm, "end": v(-7.68, -1.07) * mm});
            skLineSegment(sketch, "E352", {"start": v(-7.68, -1.07) * mm, "end": v(-7.56, -0.96) * mm});
            skLineSegment(sketch, "E353", {"start": v(-7.56, -0.96) * mm, "end": v(-7.4, -0.86) * mm});
            skLineSegment(sketch, "E354", {"start": v(-7.4, -0.86) * mm, "end": v(-7.24, -0.81) * mm});
            skLineSegment(sketch, "E355", {"start": v(-7.24, -0.81) * mm, "end": v(-7.07, -0.8) * mm});
            skLineSegment(sketch, "E356", {"start": v(-7.07, -0.8) * mm, "end": v(-6.3, -0.8) * mm});
            skLineSegment(sketch, "E357", {"start": v(-6.3, -0.8) * mm, "end": v(-6.3, 0.65) * mm});
            skLineSegment(sketch, "E358", {"start": v(-6.3, 0.65) * mm, "end": v(-7.46, 0.65) * mm});
            skLineSegment(sketch, "E359", {"start": v(-7.46, 0.65) * mm, "end": v(-7.59, 0.67) * mm});
            skLineSegment(sketch, "E360", {"start": v(-7.59, 0.67) * mm, "end": v(-7.71, 0.7) * mm});
            skLineSegment(sketch, "E361", {"start": v(-7.71, 0.7) * mm, "end": v(-7.83, 0.77) * mm});
            skLineSegment(sketch, "E362", {"start": v(-7.83, 0.77) * mm, "end": v(-7.92, 0.85) * mm});
            skLineSegment(sketch, "E363", {"start": v(-7.92, 0.85) * mm, "end": v(-8, 0.96) * mm});
            skLineSegment(sketch, "E364", {"start": v(-8, 0.96) * mm, "end": v(-8.06, 1.08) * mm});
            skLineSegment(sketch, "E365", {"start": v(-8.06, 1.08) * mm, "end": v(-8.08, 1.2) * mm});
            skLineSegment(sketch, "E366", {"start": v(-8.08, 1.2) * mm, "end": v(-8.08, 1.34) * mm});
            skLineSegment(sketch, "E367", {"start": v(-8.08, 1.34) * mm, "end": v(-8.06, 1.47) * mm});
            skLineSegment(sketch, "E368", {"start": v(-8.06, 1.47) * mm, "end": v(-8, 1.58) * mm});
            skLineSegment(sketch, "E369", {"start": v(-8, 1.58) * mm, "end": v(-7.92, 1.7) * mm});
            skLineSegment(sketch, "E370", {"start": v(-7.92, 1.7) * mm, "end": v(-7.83, 1.78) * mm});
            skLineSegment(sketch, "E371", {"start": v(-7.83, 1.78) * mm, "end": v(-7.71, 1.84) * mm});
            skLineSegment(sketch, "E372", {"start": v(-7.71, 1.84) * mm, "end": v(-7.59, 1.89) * mm});
            skLineSegment(sketch, "E373", {"start": v(-7.59, 1.89) * mm, "end": v(-7.46, 1.9) * mm});
            skLineSegment(sketch, "E374", {"start": v(-7.46, 1.9) * mm, "end": v(-6.2, 1.9) * mm});
            skLineSegment(sketch, "E375", {"start": v(-6.2, 1.9) * mm, "end": v(-6.08, 1.89) * mm});
            skLineSegment(sketch, "E376", {"start": v(-6.08, 1.89) * mm, "end": v(-5.95, 1.84) * mm});
            skLineSegment(sketch, "E377", {"start": v(-5.95, 1.84) * mm, "end": v(-5.84, 1.78) * mm});
            skLineSegment(sketch, "E378", {"start": v(-5.84, 1.78) * mm, "end": v(-5.74, 1.7) * mm});
            skLineSegment(sketch, "E379", {"start": v(-5.74, 1.7) * mm, "end": v(-5.67, 1.58) * mm});
            skLineSegment(sketch, "E380", {"start": v(-5.67, 1.58) * mm, "end": v(-5.6, 1.47) * mm});
            skLineSegment(sketch, "E381", {"start": v(-5.6, 1.47) * mm, "end": v(-5.59, 1.34) * mm});
            skLineSegment(sketch, "E382", {"start": v(-5.59, 1.34) * mm, "end": v(-5.59, 1.2) * mm});
            skLineSegment(sketch, "E383", {"start": v(-5.59, 1.2) * mm, "end": v(-5.6, 1.08) * mm});
            skLineSegment(sketch, "E384", {"start": v(-5.6, 1.08) * mm, "end": v(-5.67, 0.96) * mm});
            skLineSegment(sketch, "E385", {"start": v(-5.67, 0.96) * mm, "end": v(-5.74, 0.85) * mm});
            skLineSegment(sketch, "E386", {"start": v(-5.74, 0.85) * mm, "end": v(-5.84, 0.77) * mm});
            skLineSegment(sketch, "E387", {"start": v(-5.84, 0.77) * mm, "end": v(-5.95, 0.7) * mm});
            skLineSegment(sketch, "E388", {"start": v(-5.95, 0.7) * mm, "end": v(-6.08, 0.67) * mm});
            skLineSegment(sketch, "E389", {"start": v(-6.08, 0.67) * mm, "end": v(-6.18, 0.66) * mm});
            skLineSegment(sketch, "E390", {"start": v(-6.18, 0.66) * mm, "end": v(-6.18, -0.8) * mm});
            skSolve(sketch);
        }
        {
            var Q0;
            Q0=makeQuery(id+"F0.imprint","IMPRINT",FACE,{"disambiguationData":[TD([[makeQuery(id+"F0.imprint","IMPRINT",EDGE,{"derivedFrom":sQuery(id+"F0.wireOp",EDGE,"E51")}),-1.0]])]});
            var Q1;
            Q1=makeQuery(id+"F0.imprint","IMPRINT",FACE,{"disambiguationData":[TD([[makeQuery(id+"F0.imprint","IMPRINT",EDGE,{"derivedFrom":sQuery(id+"F0.wireOp",EDGE,"E100")}),-1.0]])]});
            var Q2;
            Q2=makeQuery(id+"F0.imprint","IMPRINT",FACE,{"disambiguationData":[TD([[makeQuery(id+"F0.imprint","IMPRINT",EDGE,{"derivedFrom":sQuery(id+"F0.wireOp",EDGE,"E120")}),-1.0]])]});
            var Q3;
            Q3=makeQuery(id+"F0.imprint","IMPRINT",FACE,{"disambiguationData":[TD([[makeQuery(id+"F0.imprint","IMPRINT",EDGE,{"derivedFrom":sQuery(id+"F0.wireOp",EDGE,"E206")}),-1.0]])]});
            var Q4;
            Q4=makeQuery(id+"F0.imprint","IMPRINT",FACE,{"disambiguationData":[TD([[makeQuery(id+"F0.imprint","IMPRINT",EDGE,{"derivedFrom":sQuery(id+"F0.wireOp",EDGE,"E0")}),-1.0]])]});
            var Q5;
            Q5=makeQuery(id+"F0.imprint","IMPRINT",FACE,{"disambiguationData":[TD([[makeQuery(id+"F0.imprint","IMPRINT",EDGE,{"derivedFrom":sQuery(id+"F0.wireOp",EDGE,"E75")}),-1.0]])]});
            var Q6;
            Q6=makeQuery(id+"F0.imprint","IMPRINT",FACE,{"disambiguationData":[TD([[makeQuery(id+"F0.imprint","IMPRINT",EDGE,{"derivedFrom":sQuery(id+"F0.wireOp",EDGE,"E293")}),-1.0]])]});
            extrude(context, id + "F1", {"entities" : qUnion([Q0, Q1, Q2, Q3, Q4, Q5, Q6]), "depth" : 0.2 * mm, "offsetDistance" : 25 * mm});
        }
    });
